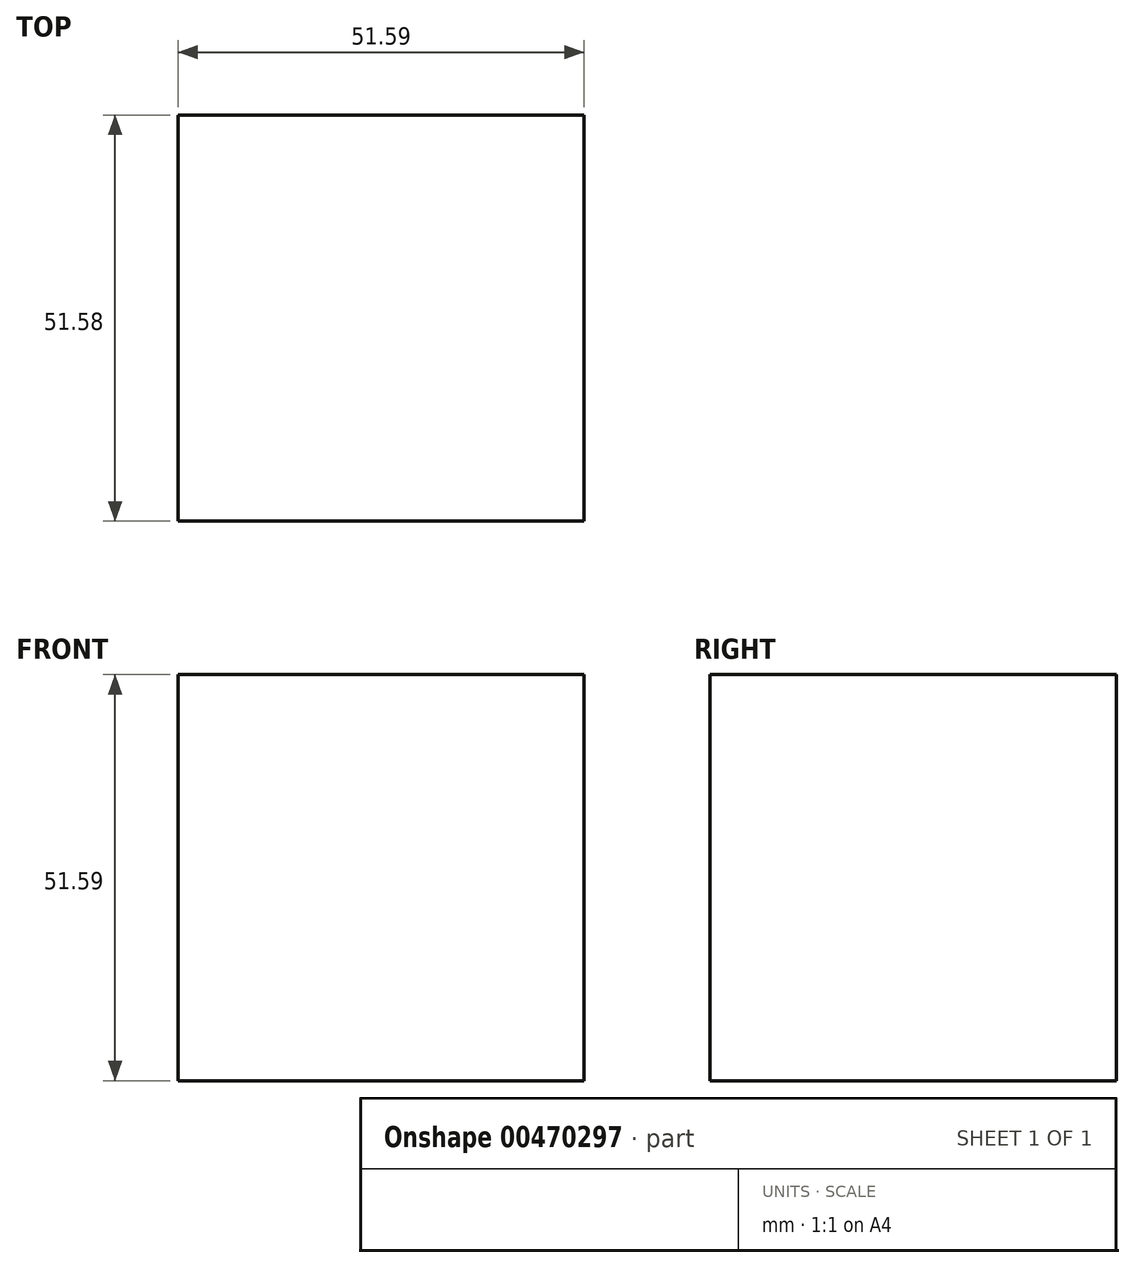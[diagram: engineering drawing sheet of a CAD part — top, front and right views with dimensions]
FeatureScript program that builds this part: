
annotation { "Feature Type Name" : "Feature", "Feature Type Description" : "" }
export const myFeature = defineFeature(function(context is Context, id is Id, definition is map)
    precondition{}
    {
        {
            var Q0;
            Q0=qCreatedBy(makeId("Top.planeOp"),FACE);
            var sketch = newSketch(context, id + "F0", { "sketchPlane" : qUnion([Q0])});
            skLineSegment(sketch, "E0.bottom", {"start": v(-24.96, 27.94) * mm, "end": v(26.63, 27.94) * mm});
            skLineSegment(sketch, "E0.top", {"start": v(-24.96, -23.64) * mm, "end": v(26.63, -23.64) * mm});
            skLineSegment(sketch, "E0.left", {"start": v(-24.96, 27.94) * mm, "end": v(-24.96, -23.64) * mm});
            skLineSegment(sketch, "E0.right", {"start": v(26.63, 27.94) * mm, "end": v(26.63, -23.64) * mm});
            skSolve(sketch);
        }
        {
            var Q0;
            Q0=makeQuery(id+"F0.imprint","IMPRINT",FACE,{"disambiguationData":[TD([[makeQuery(id+"F0.imprint","IMPRINT",EDGE,{"derivedFrom":sQuery(id+"F0.wireOp",EDGE,"E0.bottom")}),-1.0]])]});
            extrude(context, id + "F1", {"entities" : qUnion([Q0]), "depth" : 51.6 * mm});
        }
    });
